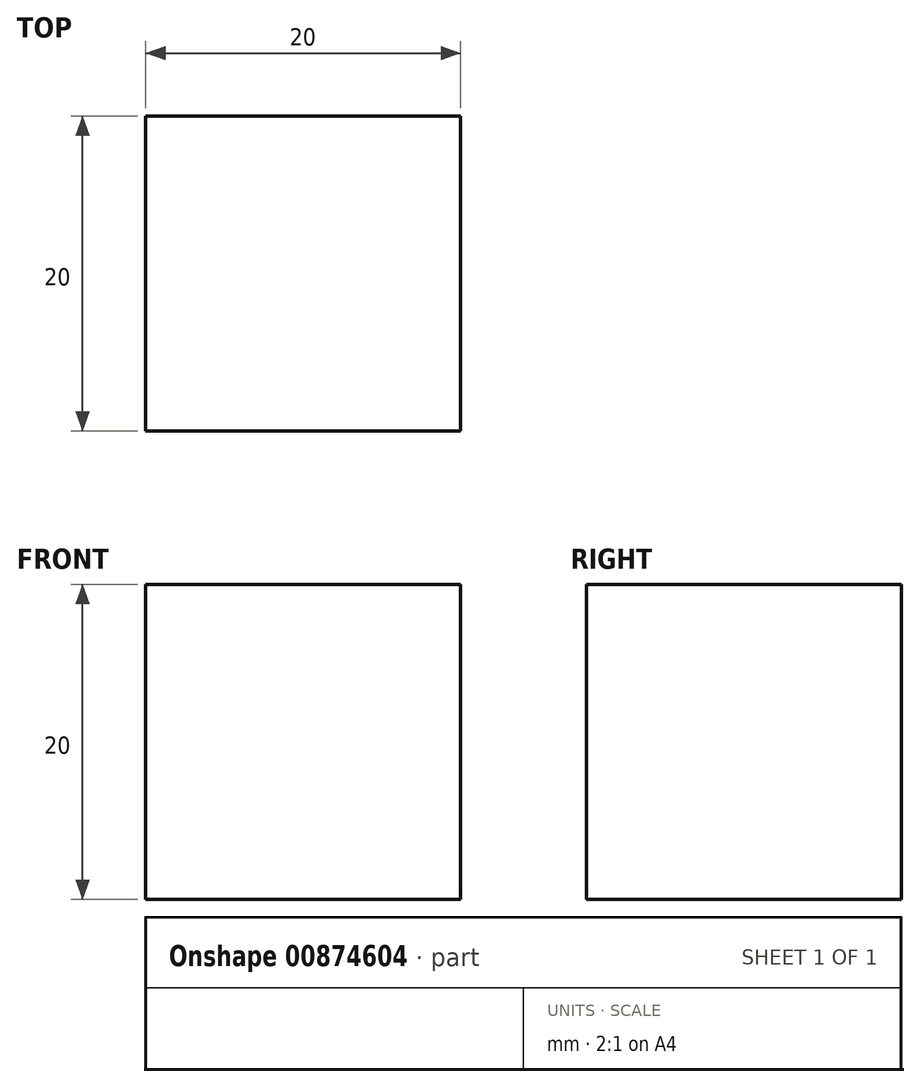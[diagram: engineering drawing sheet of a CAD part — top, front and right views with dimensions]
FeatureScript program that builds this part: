
annotation { "Feature Type Name" : "Feature", "Feature Type Description" : "" }
export const myFeature = defineFeature(function(context is Context, id is Id, definition is map)
    precondition{}
    {
        {
            var Q0;
            Q0=qCreatedBy(makeId("Top.planeOp"),FACE);
            var sketch = newSketch(context, id + "F0", { "sketchPlane" : qUnion([Q0])});
            skLineSegment(sketch, "E0.bottom", {"start": v(-39.88, -18.07) * mm, "end": v(-19.88, -18.07) * mm});
            skLineSegment(sketch, "E0.top", {"start": v(-39.88, -38.07) * mm, "end": v(-19.88, -38.07) * mm});
            skLineSegment(sketch, "E0.left", {"start": v(-39.88, -18.07) * mm, "end": v(-39.88, -38.07) * mm});
            skLineSegment(sketch, "E0.right", {"start": v(-19.88, -18.07) * mm, "end": v(-19.88, -38.07) * mm});
            skSolve(sketch);
        }
        {
            var Q0;
            Q0=makeQuery(id+"F0.imprint","IMPRINT",FACE,{"disambiguationData":[TD([[makeQuery(id+"F0.imprint","IMPRINT",EDGE,{"derivedFrom":sQuery(id+"F0.wireOp",EDGE,"E0.bottom")}),-1.0]])]});
            extrude(context, id + "F1", {"entities" : qUnion([Q0]), "depth" : 20 * mm, "offsetDistance" : 25 * mm});
        }
    });
